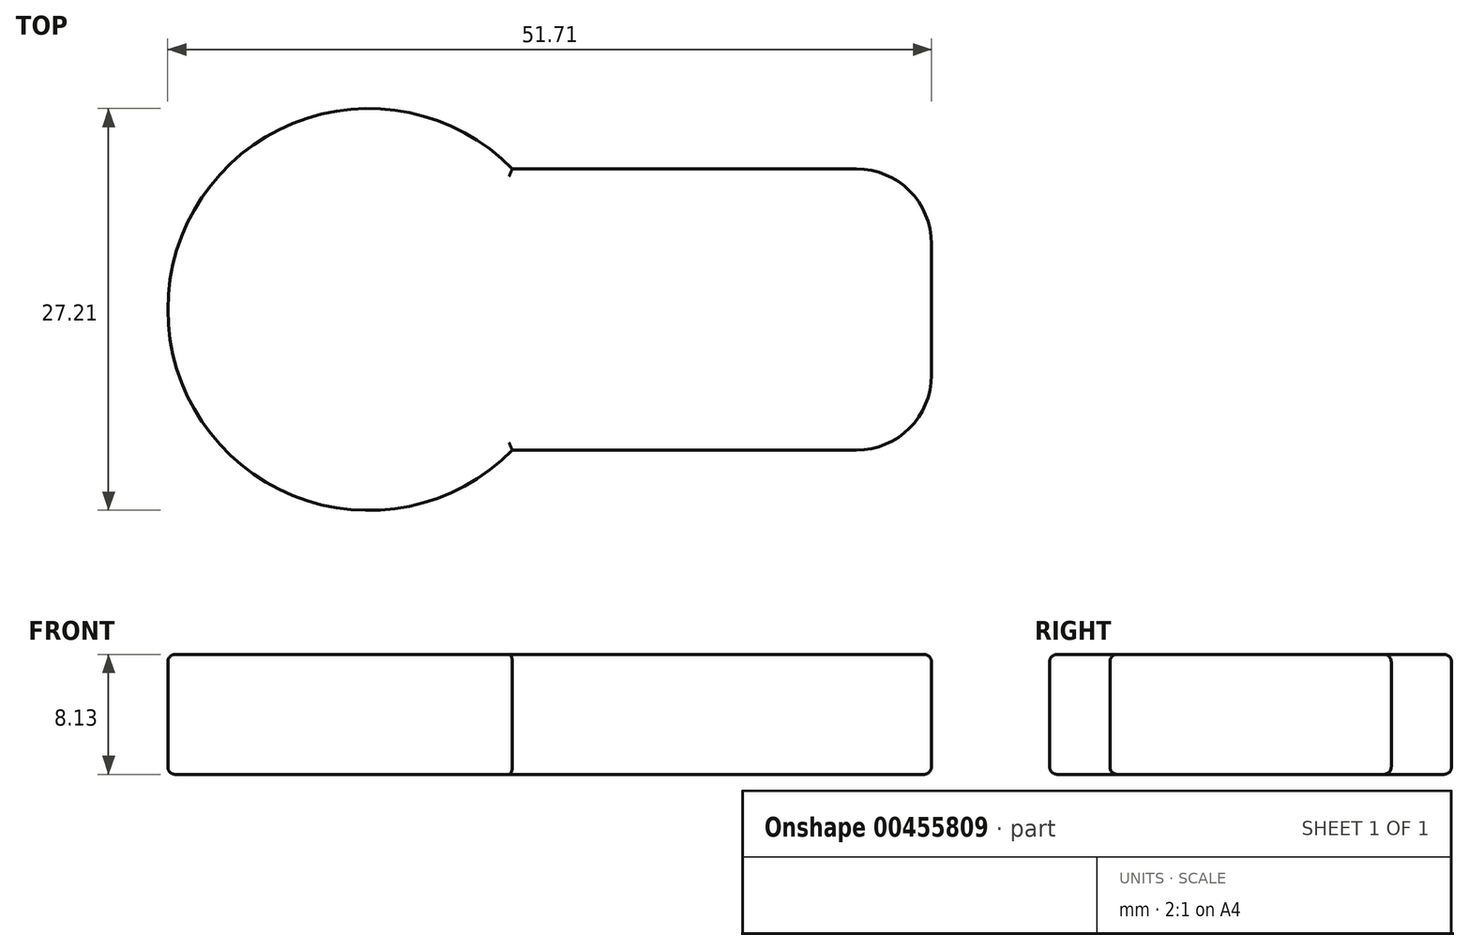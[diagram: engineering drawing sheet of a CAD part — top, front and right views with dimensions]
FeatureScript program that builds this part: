
annotation { "Feature Type Name" : "Feature", "Feature Type Description" : "" }
export const myFeature = defineFeature(function(context is Context, id is Id, definition is map)
    precondition{}
    {
        {
            var Q0;
            Q0=qCreatedBy(makeId("Top.planeOp"),FACE);
            var sketch = newSketch(context, id + "F0", { "sketchPlane" : qUnion([Q0])});
            skLineSegment(sketch, "E0.bottom", {"start": v(9.72, 0) * mm, "end": v(38.1, 0) * mm});
            skLineSegment(sketch, "E0.top", {"start": v(9.72, 19.05) * mm, "end": v(38.1, 19.05) * mm});
            skLineSegment(sketch, "E0.right", {"start": v(38.1, 0) * mm, "end": v(38.1, 19.05) * mm});
            skArc(sketch, "E1", {"start": v(9.72, 19.05) * mm, "mid": v(-13.6, 9.53) * mm, "end": v(9.72, 0) * mm});
            skPoint(sketch, "E2.orphan", {"position": v(0, 19.05) * mm});
            skPoint(sketch, "E3.orphan", {"position": v(0, 0) * mm});
            skSolve(sketch);
        }
        {
            var Q0;
            Q0 = qSketchRegion(id + "F0", true);
            extrude(context, id + "F1", {"entities" : qUnion([Q0]), "depth" : 8.13 * mm});
        }
        {
            var Q0;
            Q0=makeQuery(id+"F1.opExtrude","SWEPT_EDGE",EDGE,{"disambiguationData":[OSD([sQuery(id+"F0.wireOp",EDGE,"E0.top"),sQuery(id+"F0.wireOp",EDGE,"E0.right")])]});
            var Q1;
            Q1=makeQuery(id+"F1.opExtrude","SWEPT_EDGE",EDGE,{"disambiguationData":[OSD([sQuery(id+"F0.wireOp",EDGE,"E0.bottom"),sQuery(id+"F0.wireOp",EDGE,"E0.right")])]});
            fillet(context, id + "F2", {"entities" : qUnion([Q0, Q1]), "radius" : 5.08 * mm, "tangentPropagation" : true, "allowEdgeOverflow" : false});
        }
        {
            var Q0;
            Q0=makeQuery(id+"F1.opExtrude","CAP_EDGE",EDGE,{"disambiguationData":[OSD([sQuery(id+"F0.wireOp",EDGE,"E1")])],"isStart":false});
            var Q1;
            Q1=makeQuery(id+"F1.opExtrude","CAP_EDGE",EDGE,{"disambiguationData":[OSD([sQuery(id+"F0.wireOp",EDGE,"E0.bottom")])],"isStart":false});
            var Q2;
            {var subQ0=sQuery(id+"F0.wireOp",EDGE,"E0.right");var subQ1=sQuery(id+"F0.wireOp",EDGE,"E0.bottom");Q2=makeQuery(id+"F2.opFillet","BLEND_EDGE",EDGE,{"blendedFrom":[makeQuery(id+"F1.opExtrude","SWEPT_EDGE",EDGE,{"disambiguationData":[OSD([subQ1,subQ0])]}),makeQuery(id+"F1.opExtrude","CAP_FACE",FACE,{"disambiguationData":[OSD([subQ1,sQuery(id+"F0.wireOp",EDGE,"E0.top"),subQ0,sQuery(id+"F0.wireOp",EDGE,"E1")])],"isStart":false})],"blendedInto":[makeQuery(id+"F1.opExtrude","CAP_FACE",FACE,{"disambiguationData":[OSD([subQ1,sQuery(id+"F0.wireOp",EDGE,"E0.top"),subQ0,sQuery(id+"F0.wireOp",EDGE,"E1")])],"isStart":false})]});}
            var Q3;
            Q3=makeQuery(id+"F1.opExtrude","CAP_EDGE",EDGE,{"disambiguationData":[OSD([sQuery(id+"F0.wireOp",EDGE,"E0.right")])],"isStart":false});
            var Q4;
            {var subQ0=sQuery(id+"F0.wireOp",EDGE,"E0.right");var subQ1=sQuery(id+"F0.wireOp",EDGE,"E0.top");Q4=makeQuery(id+"F2.opFillet","BLEND_EDGE",EDGE,{"blendedFrom":[makeQuery(id+"F1.opExtrude","SWEPT_EDGE",EDGE,{"disambiguationData":[OSD([subQ1,subQ0])]}),makeQuery(id+"F1.opExtrude","CAP_FACE",FACE,{"disambiguationData":[OSD([sQuery(id+"F0.wireOp",EDGE,"E0.bottom"),subQ1,subQ0,sQuery(id+"F0.wireOp",EDGE,"E1")])],"isStart":false})],"blendedInto":[makeQuery(id+"F1.opExtrude","CAP_FACE",FACE,{"disambiguationData":[OSD([sQuery(id+"F0.wireOp",EDGE,"E0.bottom"),subQ1,subQ0,sQuery(id+"F0.wireOp",EDGE,"E1")])],"isStart":false})]});}
            var Q5;
            Q5=makeQuery(id+"F1.opExtrude","CAP_EDGE",EDGE,{"disambiguationData":[OSD([sQuery(id+"F0.wireOp",EDGE,"E0.top")])],"isStart":false});
            var Q6;
            Q6=makeQuery(id+"F1.opExtrude","CAP_EDGE",EDGE,{"disambiguationData":[OSD([sQuery(id+"F0.wireOp",EDGE,"E1")])],"isStart":true});
            var Q7;
            Q7=makeQuery(id+"F1.opExtrude","CAP_EDGE",EDGE,{"disambiguationData":[OSD([sQuery(id+"F0.wireOp",EDGE,"E0.bottom")])],"isStart":true});
            var Q8;
            Q8=makeQuery(id+"F1.opExtrude","CAP_FACE",FACE,{"disambiguationData":[OSD([sQuery(id+"F0.wireOp",EDGE,"E0.bottom"),sQuery(id+"F0.wireOp",EDGE,"E0.top"),sQuery(id+"F0.wireOp",EDGE,"E0.right"),sQuery(id+"F0.wireOp",EDGE,"E1")])],"isStart":true});
            fillet(context, id + "F3", {"entities" : qUnion([Q0, Q1, Q2, Q3, Q4, Q5, Q6, Q7, Q8]), "radius" : 0.5 * mm, "tangentPropagation" : true, "allowEdgeOverflow" : false});
        }
    });
